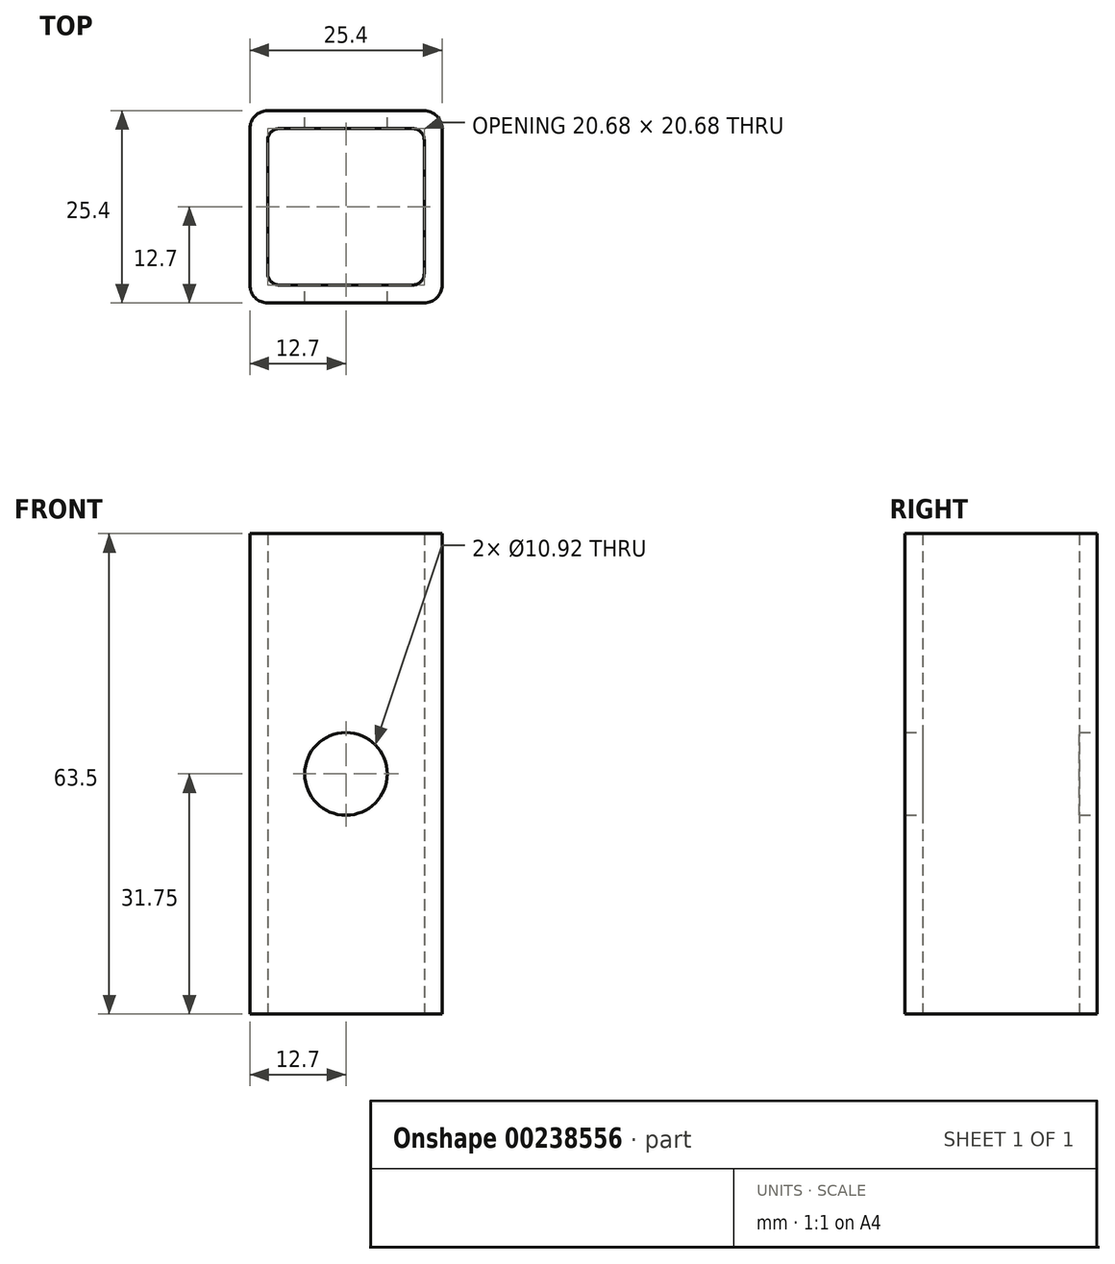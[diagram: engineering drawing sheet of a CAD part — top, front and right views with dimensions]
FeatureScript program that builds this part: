
annotation { "Feature Type Name" : "Feature", "Feature Type Description" : "" }
export const myFeature = defineFeature(function(context is Context, id is Id, definition is map)
    precondition{}
    {
        {
            var Q0;
            Q0=qCreatedBy(makeId("Top.planeOp"),FACE);
            var sketch = newSketch(context, id + "F0", { "sketchPlane" : qUnion([Q0])});
            skLineSegment(sketch, "E0", {"start": v(-12.7, 10.34) * mm, "end": v(-12.7, -10.34) * mm});
            skLineSegment(sketch, "E1", {"start": v(-10.34, -12.7) * mm, "end": v(10.34, -12.7) * mm});
            skLineSegment(sketch, "E2", {"start": v(12.7, -10.34) * mm, "end": v(12.7, 10.34) * mm});
            skLineSegment(sketch, "E3", {"start": v(10.34, 12.7) * mm, "end": v(-10.34, 12.7) * mm});
            skLineSegment(sketch, "E4", {"start": v(0, 12.7) * mm, "end": v(0, -12.7) * mm, "construction": true});
            skLineSegment(sketch, "E5", {"start": v(-12.7, 0) * mm, "end": v(12.7, 0) * mm, "construction": true});
            skPoint(sketch, "E6", {"position": v(0, 0) * mm});
            skPoint(sketch, "E7.visualSharp", {"position": v(-12.7, 12.7) * mm});
            skArc(sketch, "E7.filletArc", {"start": v(-10.34, 12.7) * mm, "mid": v(-12, 12) * mm, "end": v(-12.7, 10.34) * mm});
            skPoint(sketch, "E8.visualSharp", {"position": v(12.7, 12.7) * mm});
            skArc(sketch, "E8.filletArc", {"start": v(12.7, 10.34) * mm, "mid": v(12, 12) * mm, "end": v(10.34, 12.7) * mm});
            skPoint(sketch, "E9.visualSharp", {"position": v(12.7, -12.7) * mm});
            skArc(sketch, "E9.filletArc", {"start": v(10.34, -12.7) * mm, "mid": v(12, -12) * mm, "end": v(12.7, -10.34) * mm});
            skPoint(sketch, "E10.visualSharp", {"position": v(-12.7, -12.7) * mm});
            skArc(sketch, "E10.filletArc", {"start": v(-12.7, -10.34) * mm, "mid": v(-12, -12) * mm, "end": v(-10.34, -12.7) * mm});
            skLineSegment(sketch, "E11.0", {"start": v(8.81, 10.34) * mm, "end": v(-8.81, 10.34) * mm});
            skLineSegment(sketch, "E12.0", {"start": v(10.34, -8.81) * mm, "end": v(10.34, 8.81) * mm});
            skLineSegment(sketch, "E13.0", {"start": v(-8.81, -10.34) * mm, "end": v(8.81, -10.34) * mm});
            skLineSegment(sketch, "E14.0", {"start": v(-10.34, 8.81) * mm, "end": v(-10.34, -8.81) * mm});
            skArc(sketch, "E15.filletArc", {"start": v(-8.81, 10.34) * mm, "mid": v(-9.9, 9.9) * mm, "end": v(-10.34, 8.81) * mm});
            skArc(sketch, "E16.filletArc", {"start": v(10.34, 8.81) * mm, "mid": v(9.9, 9.9) * mm, "end": v(8.81, 10.34) * mm});
            skArc(sketch, "E17.filletArc", {"start": v(8.81, -10.34) * mm, "mid": v(9.9, -9.9) * mm, "end": v(10.34, -8.81) * mm});
            skArc(sketch, "E18.filletArc", {"start": v(-10.34, -8.81) * mm, "mid": v(-9.9, -9.9) * mm, "end": v(-8.81, -10.34) * mm});
            skSolve(sketch);
        }
        {
            var Q0;
            Q0=makeQuery(id+"F0.imprint","IMPRINT",FACE,{"disambiguationData":[TD([[makeQuery(id+"F0.imprint","IMPRINT",EDGE,{"derivedFrom":sQuery(id+"F0.wireOp",EDGE,"E0")}),1.0]])]});
            extrude(context, id + "F1", {"entities" : qUnion([Q0]), "depth" : 63.5 * mm});
        }
        {
            var Q0;
            Q0=makeQuery(id+"F1.opExtrude","SWEPT_FACE",FACE,{"disambiguationData":[OSD([sQuery(id+"F0.wireOp",EDGE,"E1")])]});
            var sketch = newSketch(context, id + "F2", { "sketchPlane" : qUnion([Q0])});
            skPoint(sketch, "E19", {"position": v(0, 31.75) * mm});
            skPoint(sketch, "E19.positionSnap0", {"position": v(0, 63.5) * mm});
            skSolve(sketch);
        }
        {
            var Q0;
            Q0=sQuery(id+"F2.wireOp",VERTEX,"E19");
            var Q1;
            Q1=makeQuery(id+"F1.opExtrude","SWEPT_BODY",BODY,{"disambiguationData":[OSD([sQuery(id+"F0.wireOp",EDGE,"E0"),sQuery(id+"F0.wireOp",EDGE,"E1"),sQuery(id+"F0.wireOp",EDGE,"E2"),sQuery(id+"F0.wireOp",EDGE,"E3"),sQuery(id+"F0.wireOp",EDGE,"E7.filletArc"),sQuery(id+"F0.wireOp",EDGE,"E8.filletArc"),sQuery(id+"F0.wireOp",EDGE,"E9.filletArc"),sQuery(id+"F0.wireOp",EDGE,"E10.filletArc"),sQuery(id+"F0.wireOp",EDGE,"E11.0"),sQuery(id+"F0.wireOp",EDGE,"E12.0"),sQuery(id+"F0.wireOp",EDGE,"E13.0"),sQuery(id+"F0.wireOp",EDGE,"E14.0"),sQuery(id+"F0.wireOp",EDGE,"E15.filletArc"),sQuery(id+"F0.wireOp",EDGE,"E16.filletArc"),sQuery(id+"F0.wireOp",EDGE,"E17.filletArc"),sQuery(id+"F0.wireOp",EDGE,"E18.filletArc")])]});
            hole(context, id + "F3", {"style" : HoleStyle.SIMPLE, "endStyle" : HoleEndStyle.THROUGH, "holeDiameter" : 10.92 * mm, "locations" : qUnion([Q0]), "scope" : qUnion([Q1]), "isTappedThrough" : true, "startStyle" : HoleStartStyle.PART});
        }
    });
